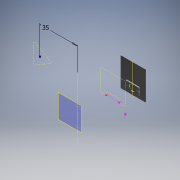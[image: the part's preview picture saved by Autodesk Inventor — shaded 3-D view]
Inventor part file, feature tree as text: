
AUTODESK INVENTOR PART (.ipt)
format: ipt  version: 2019 (Build 230136000, 136)  size: 148,992 bytes
history: native  units: mm
features: sketch x5, extrude x4, projected_geometry x3, plane x2
ambient origin geometry x8: Origin, YZ Plane, XZ Plane, XY Plane, X Axis, Y Axis, Z Axis, Center Point
bodies: Volumenkörper1 (feature_tree)
feature tree (14):
  extrude  "Extrusion1"  Depth=26.8mm
  extrude  "Extrusion2"  Depth=3.0mm
  extrude  "Extrusion3"  Depth=5.5mm
  plane  "Work Plane1"
  extrude  "Extrusion5"  Depth=1.0mm TaperAngle=0.0deg
  plane  "Work Plane3"
  sketch  "Sketch6"  dims[d10=1.0mm d11=0.0mm d14=10.0mm d15=0.0mm d16=35.0mm]
  sketch  "Skizze1"  dims[d0=23.3mm d1=26.8mm]
  sketch  "Skizze2"  dims[d2=0.4mm d3=0.0mm d4=3.0mm]
  projected_geometry  "Projizierte Kontur1"
  sketch  "Skizze3"  dims[d5=17.0mm d6=5.5mm]
  projected_geometry  "Projizierte Kontur2"
  sketch  "Sketch5"  dims[d7=5.5mm d8=1.0mm d9=0.0mm]
  projected_geometry  "Projected Loop4"
